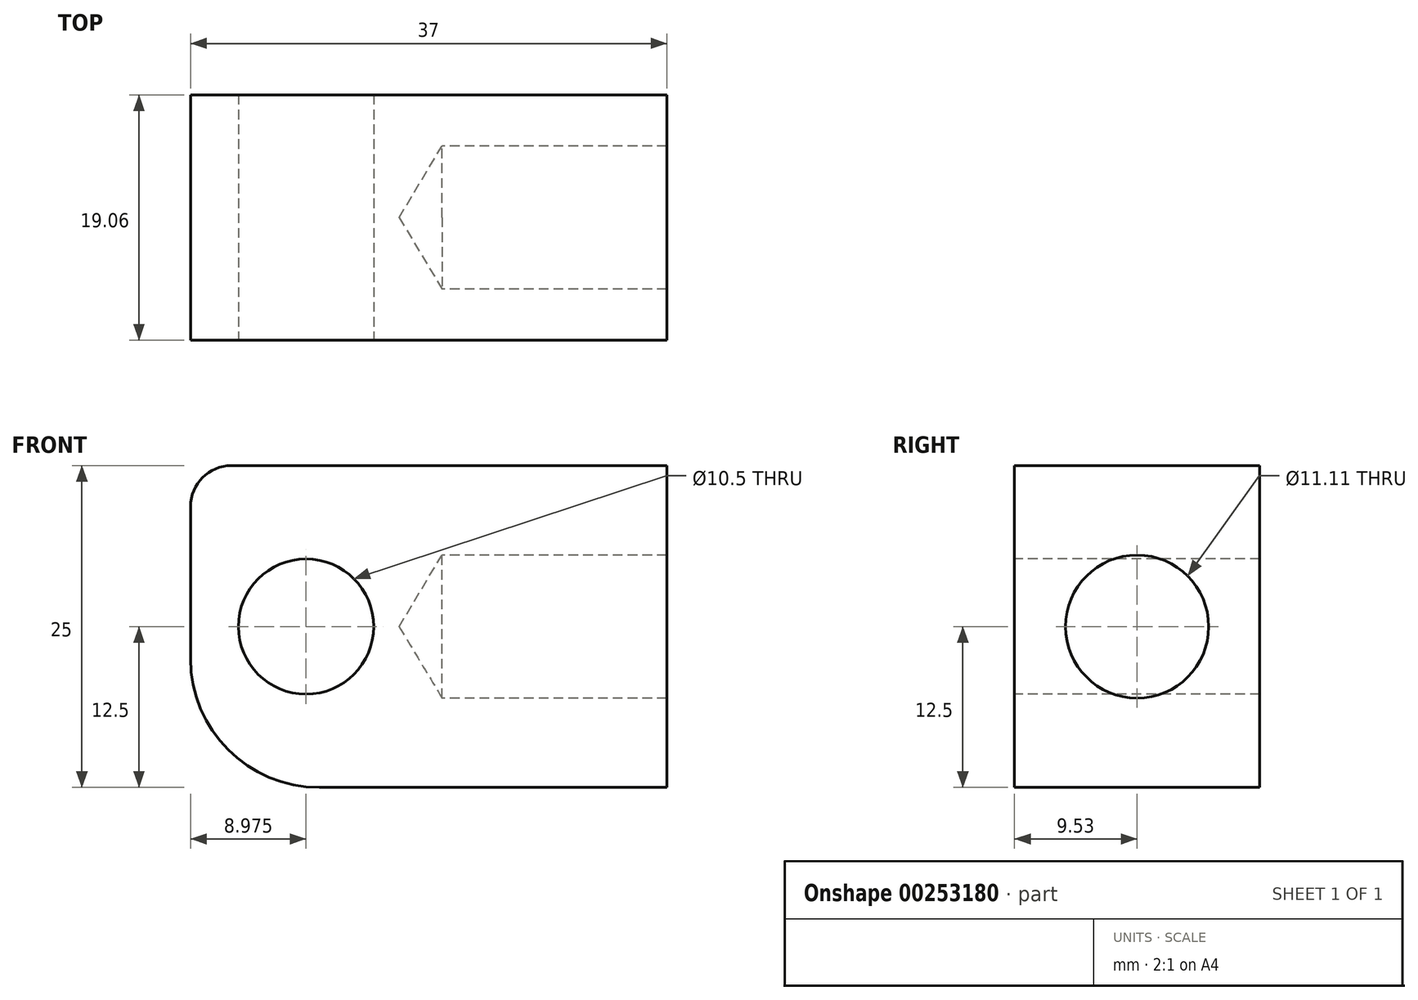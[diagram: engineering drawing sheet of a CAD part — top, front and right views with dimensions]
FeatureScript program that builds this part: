
annotation { "Feature Type Name" : "Feature", "Feature Type Description" : "" }
export const myFeature = defineFeature(function(context is Context, id is Id, definition is map)
    precondition{}
    {
        {
            var Q0;
            Q0=qCreatedBy(makeId("Front.planeOp"),FACE);
            var sketch = newSketch(context, id + "F0", { "sketchPlane" : qUnion([Q0])});
            skLineSegment(sketch, "E0.rect.bottom", {"start": v(-18.5, -12.5) * mm, "end": v(18.5, -12.5) * mm});
            skLineSegment(sketch, "E0.rect.top", {"start": v(-18.5, 12.5) * mm, "end": v(18.5, 12.5) * mm});
            skLineSegment(sketch, "E0.rect.left", {"start": v(-18.5, -12.5) * mm, "end": v(-18.5, 12.5) * mm});
            skLineSegment(sketch, "E0.rect.right", {"start": v(18.5, -12.5) * mm, "end": v(18.5, 12.5) * mm});
            skSolve(sketch);
        }
        {
            var Q0;
            Q0=qCreatedBy(makeId("Front.planeOp"),FACE);
            var sketch = newSketch(context, id + "F1", { "sketchPlane" : qUnion([Q0])});
            skCircle(sketch, "E1", {"center": v(-9.53, 0) * mm, "radius": 5.25 * mm});
            skSolve(sketch);
        }
        {
            var Q0;
            Q0=makeQuery(id+"F0.imprint","IMPRINT",FACE,{"disambiguationData":[TD([[makeQuery(id+"F0.imprint","IMPRINT",EDGE,{"derivedFrom":sQuery(id+"F0.wireOp",EDGE,"E0.rect.bottom")}),1.0]])]});
            extrude(context, id + "F2", {"entities" : qUnion([Q0]), "depth" : 19.05 * mm, "symmetric" : true});
        }
        {
            var Q0;
            Q0=qSketchRegion(id+"F1",true);
            extrude(context, id + "F3", {"entities" : qUnion([Q0]), "operationType" : NewBodyOperationType.REMOVE, "oppositeDirection" : true, "depth" : 25 * mm, "symmetric" : true});
        }
        {
            var Q0;
            Q0=makeQuery(id+"F2.opExtrude","SWEPT_EDGE",EDGE,{"disambiguationData":[OSD([sQuery(id+"F0.wireOp",EDGE,"E0.rect.bottom"),sQuery(id+"F0.wireOp",EDGE,"E0.rect.left")])]});
            fillet(context, id + "F4", {"entities" : qUnion([Q0]), "radius" : 10 * mm, "tangentPropagation" : true, "allowEdgeOverflow" : false});
        }
        {
            var Q0;
            Q0=makeQuery(id+"F2.opExtrude","SWEPT_FACE",FACE,{"disambiguationData":[OSD([sQuery(id+"F0.wireOp",EDGE,"E0.rect.right")])]});
            var sketch = newSketch(context, id + "F5", { "sketchPlane" : qUnion([Q0])});
            skCircle(sketch, "E2", {"center": v(0, 0) * mm, "radius": 0.19 * mm});
            skSolve(sketch);
        }
        {
            var Q0;
            Q0=sQuery(id+"F5.wireOp",VERTEX,"E2.center");
            var Q1;
            Q1=makeQuery(id+"F2.opExtrude","SWEPT_BODY",BODY,{"disambiguationData":[OSD([sQuery(id+"F0.wireOp",EDGE,"E0.rect.bottom"),sQuery(id+"F0.wireOp",EDGE,"E0.rect.top"),sQuery(id+"F0.wireOp",EDGE,"E0.rect.left"),sQuery(id+"F0.wireOp",EDGE,"E0.rect.right")])]});
            hole(context, id + "F6", {"style" : HoleStyle.SIMPLE, "holeDiameter" : 11.1 * mm, "endStyle" : HoleEndStyle.BLIND, "holeDepth" : 17.46 * mm, "locations" : qUnion([Q0]), "scope" : qUnion([Q1])});
        }
        {
            var Q0;
            Q0=makeQuery(id+"F2.opExtrude","SWEPT_EDGE",EDGE,{"disambiguationData":[OSD([sQuery(id+"F0.wireOp",EDGE,"E0.rect.top"),sQuery(id+"F0.wireOp",EDGE,"E0.rect.left")])]});
            fillet(context, id + "F7", {"entities" : qUnion([Q0]), "radius" : 3.17 * mm, "tangentPropagation" : true, "allowEdgeOverflow" : false});
        }
    });
